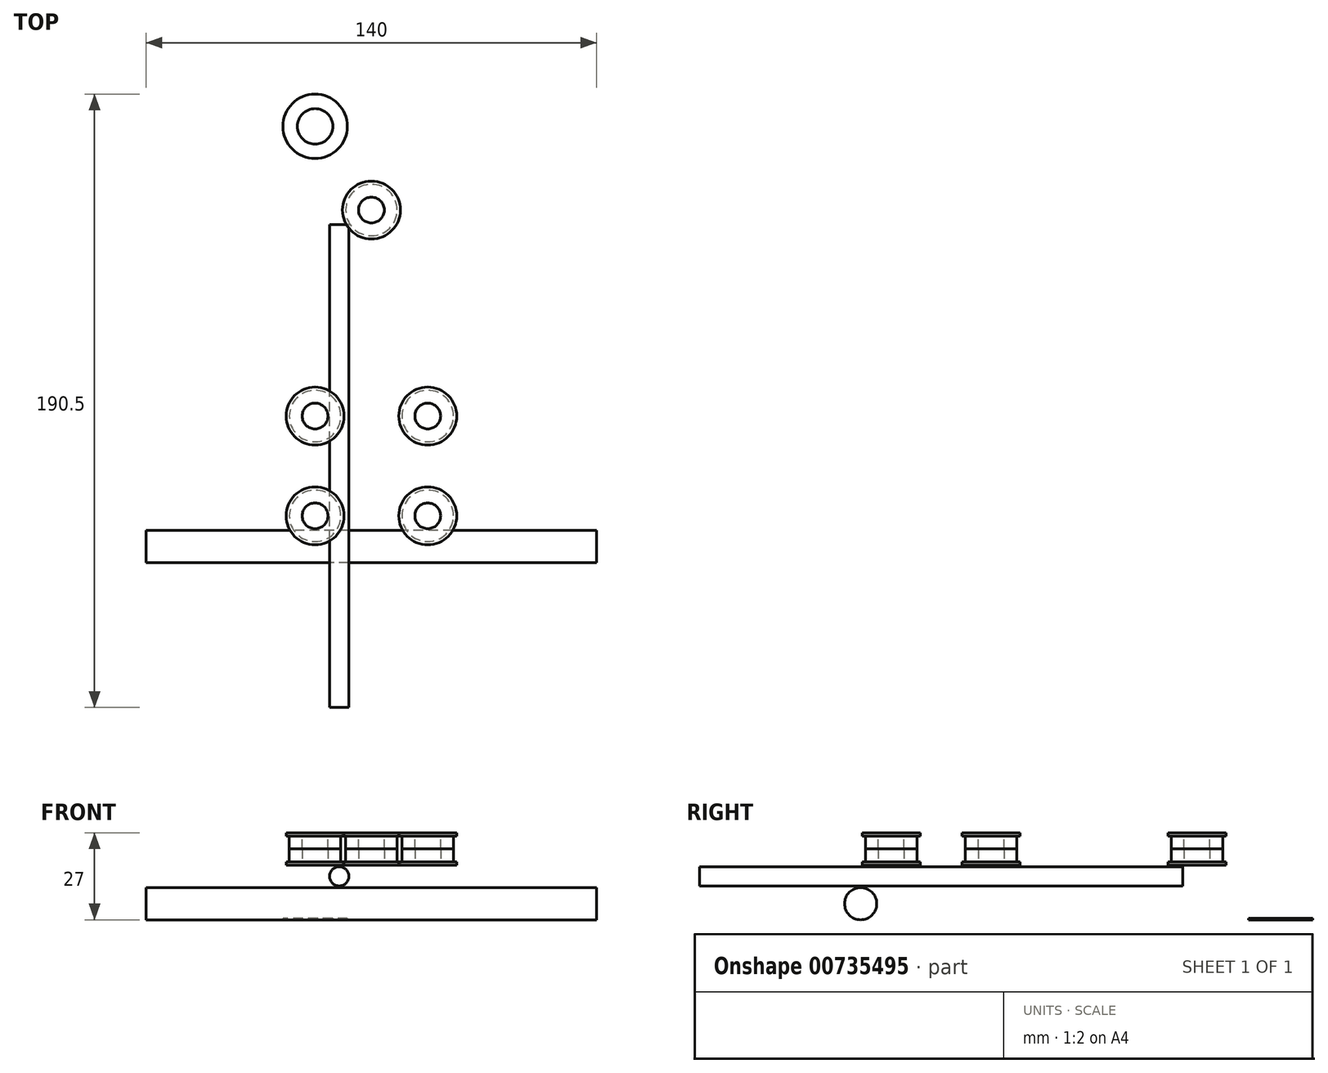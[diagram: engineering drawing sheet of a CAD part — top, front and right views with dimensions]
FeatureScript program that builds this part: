
annotation { "Feature Type Name" : "Feature", "Feature Type Description" : "" }
export const myFeature = defineFeature(function(context is Context, id is Id, definition is map)
    precondition{}
    {
        {
            var Q0;
            Q0=qCreatedBy(makeId("Right.planeOp"),FACE);
            var sketch = newSketch(context, id + "F0", { "sketchPlane" : qUnion([Q0])});
            skCircle(sketch, "E0", {"center": v(-25, 5) * mm, "radius": 5 * mm});
            skCircle(sketch, "E1.MirrorC", {"center": v(25, 5) * mm, "radius": 5 * mm});
            skCircle(sketch, "E2", {"center": v(-52.9, 19.58) * mm, "radius": 5 * mm});
            skCircle(sketch, "E3", {"center": v(-52.9, 19.58) * mm, "radius": 9.5 * mm});
            skCircle(sketch, "E4", {"center": v(-52.9, 19.58) * mm, "radius": 9.05 * mm});
            skSolve(sketch);
        }
        {
            var Q0;
            Q0=makeQuery(id+"F0.imprint","IMPRINT",FACE,{"disambiguationData":[TD([[makeQuery(id+"F0.imprint","IMPRINT",EDGE,{"derivedFrom":sQuery(id+"F0.wireOp",EDGE,"E0")}),1.0]])]});
            var Q1;
            Q1=makeQuery(id+"F0.imprint","IMPRINT",FACE,{"disambiguationData":[TD([[makeQuery(id+"F0.imprint","IMPRINT",EDGE,{"derivedFrom":sQuery(id+"F0.wireOp",EDGE,"E1.MirrorC")}),-1.0]])]});
            extrude(context, id + "F1", {"entities" : qUnion([Q0, Q1]), "endBound" : BoundingType.SYMMETRIC, "depth" : 140 * mm, "offsetDistance" : 25 * mm});
        }
        {
            var Q0;
            Q0=qCreatedBy(makeId("Front.planeOp"),FACE);
            var sketch = newSketch(context, id + "F2", { "sketchPlane" : qUnion([Q0])});
            skCircle(sketch, "E5", {"center": v(-10, 13.5) * mm, "radius": 3 * mm});
            skCircle(sketch, "E6.MirrorC", {"center": v(10, 13.5) * mm, "radius": 3 * mm});
            skLineSegment(sketch, "E7", {"start": v(-71.81, 0) * mm, "end": v(66.77, 0) * mm});
            skCircle(sketch, "E8", {"center": v(-31.3, 26.16) * mm, "radius": 3 * mm});
            skCircle(sketch, "E9", {"center": v(-31.3, 26.16) * mm, "radius": 5.7 * mm});
            skCircle(sketch, "E10", {"center": v(-31.3, 26.16) * mm, "radius": 6 * mm});
            skSolve(sketch);
        }
        {
            var Q0;
            Q0=makeQuery(id+"F2.imprint","IMPRINT",FACE,{"disambiguationData":[TD([[makeQuery(id+"F2.imprint","IMPRINT",EDGE,{"derivedFrom":sQuery(id+"F2.wireOp",EDGE,"E5")}),1.0]])]});
            var Q1;
            Q1=makeQuery(id+"F2.imprint","IMPRINT",FACE,{"disambiguationData":[TD([[makeQuery(id+"F2.imprint","IMPRINT",EDGE,{"derivedFrom":sQuery(id+"F2.wireOp",EDGE,"E6.MirrorC")}),-1.0]])]});
            extrude(context, id + "F3", {"entities" : qUnion([Q0, Q1]), "endBound" : BoundingType.SYMMETRIC, "depth" : 150 * mm, "offsetDistance" : 25 * mm});
        }
        {
            var Q0;
            Q0=qCreatedBy(makeId("Top.planeOp"),FACE);
            var sketch = newSketch(context, id + "F4", { "sketchPlane" : qUnion([Q0])});
            skCircle(sketch, "E11", {"center": v(-17.5, 15.5) * mm, "radius": 4 * mm});
            skCircle(sketch, "E12", {"center": v(-17.5, 15.5) * mm, "radius": 8 * mm});
            skCircle(sketch, "E13", {"center": v(-17.5, 15.5) * mm, "radius": 9 * mm});
            skCircle(sketch, "E14", {"center": v(-17.5, 15.5) * mm, "radius": 5.5 * mm});
            skCircle(sketch, "E15", {"center": v(-17.5, 15.5) * mm, "radius": 10 * mm});
            skSolve(sketch);
        }
        {
            var Q0;
            Q0=makeQuery(id+"F4.imprint","IMPRINT",FACE,{"disambiguationData":[TD([[makeQuery(id+"F4.imprint","IMPRINT",EDGE,{"derivedFrom":sQuery(id+"F4.wireOp",EDGE,"E12")}),-1.0]])]});
            extrude(context, id + "F5", {"entities" : qUnion([Q0]), "depth" : 1 * mm, "offsetDistance" : 25 * mm});
        }
        {
            var Q0;
            Q0=makeQuery(id+"F4.imprint","IMPRINT",FACE,{"disambiguationData":[TD([[makeQuery(id+"F4.imprint","IMPRINT",EDGE,{"derivedFrom":sQuery(id+"F4.wireOp",EDGE,"E11")}),-1.0]])]});
            var Q1;
            Q1=makeQuery(id+"F4.imprint","IMPRINT",FACE,{"disambiguationData":[TD([[makeQuery(id+"F4.imprint","IMPRINT",EDGE,{"derivedFrom":sQuery(id+"F4.wireOp",EDGE,"E12")}),1.0]])]});
            extrude(context, id + "F6", {"entities" : qUnion([Q0, Q1]), "operationType" : NewBodyOperationType.ADD, "depth" : 5 * mm, "offsetDistance" : 25 * mm});
        }
        {
            var Q0;
            Q0=makeQuery(id+"F5.opExtrude","SWEPT_BODY",BODY,{"disambiguationData":[OSD([sQuery(id+"F4.wireOp",EDGE,"E12"),sQuery(id+"F4.wireOp",EDGE,"E13")])]});
            transform(context, id + "F7", {"entities" : qUnion([Q0]), "transformType" : TransformType.TRANSLATION_3D, "dx" : 17.5 * 2 * mm, "dy" : 0 * mm, "dz" : 0 * mm, "makeCopy" : true});
        }
        {
            var Q0;
            Q0=makeQuery(id+"F5.opExtrude","SWEPT_BODY",BODY,{"disambiguationData":[OSD([sQuery(id+"F4.wireOp",EDGE,"E12"),sQuery(id+"F4.wireOp",EDGE,"E13")])]});
            var Q1;
            Q1=makeQuery(id+"F7.opPattern","COPY",BODY,{"derivedFrom":makeQuery(id+"F5.opExtrude","SWEPT_BODY",BODY,{"disambiguationData":[OSD([sQuery(id+"F4.wireOp",EDGE,"E12"),sQuery(id+"F4.wireOp",EDGE,"E13")])]}),"instanceName":"1"});
            transform(context, id + "F8", {"entities" : qUnion([Q0, Q1]), "transformType" : TransformType.TRANSLATION_3D, "dx" : 0 * mm, "dy" : -15.5 * 2 * mm, "dz" : 0 * mm, "makeCopy" : true});
        }
        {
            var Q0;
            Q0=makeQuery(id+"F5.opExtrude","SWEPT_BODY",BODY,{"disambiguationData":[OSD([sQuery(id+"F4.wireOp",EDGE,"E12"),sQuery(id+"F4.wireOp",EDGE,"E13")])]});
            var Q1;
            Q1=makeQuery(id+"F7.opPattern","COPY",BODY,{"derivedFrom":makeQuery(id+"F5.opExtrude","SWEPT_BODY",BODY,{"disambiguationData":[OSD([sQuery(id+"F4.wireOp",EDGE,"E12"),sQuery(id+"F4.wireOp",EDGE,"E13")])]}),"instanceName":"1"});
            var Q2;
            Q2=makeQuery(id+"F8.opPattern","COPY",BODY,{"derivedFrom":makeQuery(id+"F7.opPattern","COPY",BODY,{"derivedFrom":makeQuery(id+"F5.opExtrude","SWEPT_BODY",BODY,{"disambiguationData":[OSD([sQuery(id+"F4.wireOp",EDGE,"E12"),sQuery(id+"F4.wireOp",EDGE,"E13")])]}),"instanceName":"1"}),"instanceName":"1"});
            var Q3;
            Q3=makeQuery(id+"F8.opPattern","COPY",BODY,{"derivedFrom":makeQuery(id+"F5.opExtrude","SWEPT_BODY",BODY,{"disambiguationData":[OSD([sQuery(id+"F4.wireOp",EDGE,"E12"),sQuery(id+"F4.wireOp",EDGE,"E13")])]}),"instanceName":"1"});
            var Q4;
            Q4=sQuery(id+"F2.wireOp",EDGE,"E7");
            transform(context, id + "F9", {"entities" : qUnion([Q0, Q1, Q2, Q3]), "transformType" : TransformType.ROTATION, "transformAxis" : qUnion([Q4]), "angle" : 180 * degree, "makeCopy" : true});
        }
        {
            var Q0;
            Q0=makeQuery(id+"F9.opPattern","COPY",BODY,{"derivedFrom":makeQuery(id+"F8.opPattern","COPY",BODY,{"derivedFrom":makeQuery(id+"F5.opExtrude","SWEPT_BODY",BODY,{"disambiguationData":[OSD([sQuery(id+"F4.wireOp",EDGE,"E12"),sQuery(id+"F4.wireOp",EDGE,"E13")])]}),"instanceName":"1"}),"instanceName":"1"});
            var Q1;
            Q1=makeQuery(id+"F9.opPattern","COPY",BODY,{"derivedFrom":makeQuery(id+"F5.opExtrude","SWEPT_BODY",BODY,{"disambiguationData":[OSD([sQuery(id+"F4.wireOp",EDGE,"E12"),sQuery(id+"F4.wireOp",EDGE,"E13")])]}),"instanceName":"1"});
            var Q2;
            Q2=makeQuery(id+"F9.opPattern","COPY",BODY,{"derivedFrom":makeQuery(id+"F7.opPattern","COPY",BODY,{"derivedFrom":makeQuery(id+"F5.opExtrude","SWEPT_BODY",BODY,{"disambiguationData":[OSD([sQuery(id+"F4.wireOp",EDGE,"E12"),sQuery(id+"F4.wireOp",EDGE,"E13")])]}),"instanceName":"1"}),"instanceName":"1"});
            var Q3;
            Q3=makeQuery(id+"F9.opPattern","COPY",BODY,{"derivedFrom":makeQuery(id+"F8.opPattern","COPY",BODY,{"derivedFrom":makeQuery(id+"F7.opPattern","COPY",BODY,{"derivedFrom":makeQuery(id+"F5.opExtrude","SWEPT_BODY",BODY,{"disambiguationData":[OSD([sQuery(id+"F4.wireOp",EDGE,"E12"),sQuery(id+"F4.wireOp",EDGE,"E13")])]}),"instanceName":"1"}),"instanceName":"1"}),"instanceName":"1"});
            transform(context, id + "F10", {"entities" : qUnion([Q0, Q1, Q2, Q3]), "transformType" : TransformType.TRANSLATION_3D, "dx" : 0 * mm, "dy" : 0 * mm, "dz" : 27 * mm, "makeCopy" : false});
        }
        {
            var Q0;
            Q0=makeQuery(id+"F8.opPattern","COPY",BODY,{"derivedFrom":makeQuery(id+"F7.opPattern","COPY",BODY,{"derivedFrom":makeQuery(id+"F5.opExtrude","SWEPT_BODY",BODY,{"disambiguationData":[OSD([sQuery(id+"F4.wireOp",EDGE,"E12"),sQuery(id+"F4.wireOp",EDGE,"E13")])]}),"instanceName":"1"}),"instanceName":"1"});
            var Q1;
            Q1=makeQuery(id+"F7.opPattern","COPY",BODY,{"derivedFrom":makeQuery(id+"F5.opExtrude","SWEPT_BODY",BODY,{"disambiguationData":[OSD([sQuery(id+"F4.wireOp",EDGE,"E12"),sQuery(id+"F4.wireOp",EDGE,"E13")])]}),"instanceName":"1"});
            var Q2;
            Q2=makeQuery(id+"F5.opExtrude","SWEPT_BODY",BODY,{"disambiguationData":[OSD([sQuery(id+"F4.wireOp",EDGE,"E12"),sQuery(id+"F4.wireOp",EDGE,"E13")])]});
            var Q3;
            Q3=makeQuery(id+"F8.opPattern","COPY",BODY,{"derivedFrom":makeQuery(id+"F5.opExtrude","SWEPT_BODY",BODY,{"disambiguationData":[OSD([sQuery(id+"F4.wireOp",EDGE,"E12"),sQuery(id+"F4.wireOp",EDGE,"E13")])]}),"instanceName":"1"});
            transform(context, id + "F11", {"entities" : qUnion([Q0, Q1, Q2, Q3]), "transformType" : TransformType.TRANSLATION_3D, "dx" : 0 * mm, "dy" : 0 * mm, "dz" : 17 * mm, "makeCopy" : false});
        }
        {
            var Q0;
            Q0=makeQuery(id+"F9.opPattern","COPY",BODY,{"derivedFrom":makeQuery(id+"F8.opPattern","COPY",BODY,{"derivedFrom":makeQuery(id+"F5.opExtrude","SWEPT_BODY",BODY,{"disambiguationData":[OSD([sQuery(id+"F4.wireOp",EDGE,"E12"),sQuery(id+"F4.wireOp",EDGE,"E13")])]}),"instanceName":"1"}),"instanceName":"1"});
            transform(context, id + "F12", {"entities" : qUnion([Q0]), "transformType" : TransformType.TRANSLATION_3D, "dx" : 17.5 * mm, "dy" : 64 * mm, "dz" : 0 * mm, "makeCopy" : true});
        }
        {
            var Q0;
            Q0=makeQuery(id+"F12.opPattern","COPY",BODY,{"derivedFrom":makeQuery(id+"F9.opPattern","COPY",BODY,{"derivedFrom":makeQuery(id+"F8.opPattern","COPY",BODY,{"derivedFrom":makeQuery(id+"F5.opExtrude","SWEPT_BODY",BODY,{"disambiguationData":[OSD([sQuery(id+"F4.wireOp",EDGE,"E12"),sQuery(id+"F4.wireOp",EDGE,"E13")])]}),"instanceName":"1"}),"instanceName":"1"}),"instanceName":"1"});
            var Q1;
            Q1=sQuery(id+"F2.wireOp",EDGE,"E7");
            transform(context, id + "F13", {"entities" : qUnion([Q0]), "transformType" : TransformType.ROTATION, "transformAxis" : qUnion([Q1]), "angle" : 180 * degree, "makeCopy" : true});
        }
        {
            var Q0;
            Q0=makeQuery(id+"F13.opPattern","COPY",BODY,{"derivedFrom":makeQuery(id+"F12.opPattern","COPY",BODY,{"derivedFrom":makeQuery(id+"F9.opPattern","COPY",BODY,{"derivedFrom":makeQuery(id+"F8.opPattern","COPY",BODY,{"derivedFrom":makeQuery(id+"F5.opExtrude","SWEPT_BODY",BODY,{"disambiguationData":[OSD([sQuery(id+"F4.wireOp",EDGE,"E12"),sQuery(id+"F4.wireOp",EDGE,"E13")])]}),"instanceName":"1"}),"instanceName":"1"}),"instanceName":"1"}),"instanceName":"1"});
            transform(context, id + "F14", {"entities" : qUnion([Q0]), "transformType" : TransformType.TRANSLATION_3D, "dx" : 0 * mm, "dy" : 159 * mm, "dz" : 44 * mm, "makeCopy" : false});
        }
        {
            var Q0;
            Q0=makeQuery(id+"F13.opPattern","COPY",BODY,{"derivedFrom":makeQuery(id+"F12.opPattern","COPY",BODY,{"derivedFrom":makeQuery(id+"F9.opPattern","COPY",BODY,{"derivedFrom":makeQuery(id+"F8.opPattern","COPY",BODY,{"derivedFrom":makeQuery(id+"F5.opExtrude","SWEPT_BODY",BODY,{"disambiguationData":[OSD([sQuery(id+"F4.wireOp",EDGE,"E12"),sQuery(id+"F4.wireOp",EDGE,"E13")])]}),"instanceName":"1"}),"instanceName":"1"}),"instanceName":"1"}),"instanceName":"1"});
            var Q1;
            Q1=makeQuery(id+"F3.opExtrude","SWEPT_BODY",BODY,{"disambiguationData":[OSD([sQuery(id+"F2.wireOp",EDGE,"E5")])]});
            var Q2;
            Q2=makeQuery(id+"F12.opPattern","COPY",BODY,{"derivedFrom":makeQuery(id+"F9.opPattern","COPY",BODY,{"derivedFrom":makeQuery(id+"F8.opPattern","COPY",BODY,{"derivedFrom":makeQuery(id+"F5.opExtrude","SWEPT_BODY",BODY,{"disambiguationData":[OSD([sQuery(id+"F4.wireOp",EDGE,"E12"),sQuery(id+"F4.wireOp",EDGE,"E13")])]}),"instanceName":"1"}),"instanceName":"1"}),"instanceName":"1"});
            var Q3;
            Q3=makeQuery(id+"F7.opPattern","COPY",BODY,{"derivedFrom":makeQuery(id+"F5.opExtrude","SWEPT_BODY",BODY,{"disambiguationData":[OSD([sQuery(id+"F4.wireOp",EDGE,"E12"),sQuery(id+"F4.wireOp",EDGE,"E13")])]}),"instanceName":"1"});
            var Q4;
            Q4=makeQuery(id+"F3.opExtrude","SWEPT_BODY",BODY,{"disambiguationData":[OSD([sQuery(id+"F2.wireOp",EDGE,"E6.MirrorC")])]});
            var Q5;
            Q5=makeQuery(id+"F9.opPattern","COPY",BODY,{"derivedFrom":makeQuery(id+"F8.opPattern","COPY",BODY,{"derivedFrom":makeQuery(id+"F7.opPattern","COPY",BODY,{"derivedFrom":makeQuery(id+"F5.opExtrude","SWEPT_BODY",BODY,{"disambiguationData":[OSD([sQuery(id+"F4.wireOp",EDGE,"E12"),sQuery(id+"F4.wireOp",EDGE,"E13")])]}),"instanceName":"1"}),"instanceName":"1"}),"instanceName":"1"});
            var Q6;
            Q6=makeQuery(id+"F1.opExtrude","SWEPT_BODY",BODY,{"disambiguationData":[OSD([sQuery(id+"F0.wireOp",EDGE,"E1.MirrorC")])]});
            var Q7;
            Q7=makeQuery(id+"F1.opExtrude","SWEPT_BODY",BODY,{"disambiguationData":[OSD([sQuery(id+"F0.wireOp",EDGE,"E0")])]});
            var Q8;
            Q8=makeQuery(id+"F5.opExtrude","SWEPT_BODY",BODY,{"disambiguationData":[OSD([sQuery(id+"F4.wireOp",EDGE,"E12"),sQuery(id+"F4.wireOp",EDGE,"E13")])]});
            var Q9;
            Q9=makeQuery(id+"F8.opPattern","COPY",BODY,{"derivedFrom":makeQuery(id+"F5.opExtrude","SWEPT_BODY",BODY,{"disambiguationData":[OSD([sQuery(id+"F4.wireOp",EDGE,"E12"),sQuery(id+"F4.wireOp",EDGE,"E13")])]}),"instanceName":"1"});
            var Q10;
            Q10=makeQuery(id+"F8.opPattern","COPY",BODY,{"derivedFrom":makeQuery(id+"F7.opPattern","COPY",BODY,{"derivedFrom":makeQuery(id+"F5.opExtrude","SWEPT_BODY",BODY,{"disambiguationData":[OSD([sQuery(id+"F4.wireOp",EDGE,"E12"),sQuery(id+"F4.wireOp",EDGE,"E13")])]}),"instanceName":"1"}),"instanceName":"1"});
            var Q11;
            Q11=makeQuery(id+"F9.opPattern","COPY",BODY,{"derivedFrom":makeQuery(id+"F5.opExtrude","SWEPT_BODY",BODY,{"disambiguationData":[OSD([sQuery(id+"F4.wireOp",EDGE,"E12"),sQuery(id+"F4.wireOp",EDGE,"E13")])]}),"instanceName":"1"});
            var Q12;
            Q12=makeQuery(id+"F9.opPattern","COPY",BODY,{"derivedFrom":makeQuery(id+"F7.opPattern","COPY",BODY,{"derivedFrom":makeQuery(id+"F5.opExtrude","SWEPT_BODY",BODY,{"disambiguationData":[OSD([sQuery(id+"F4.wireOp",EDGE,"E12"),sQuery(id+"F4.wireOp",EDGE,"E13")])]}),"instanceName":"1"}),"instanceName":"1"});
            var Q13;
            Q13=makeQuery(id+"F9.opPattern","COPY",BODY,{"derivedFrom":makeQuery(id+"F8.opPattern","COPY",BODY,{"derivedFrom":makeQuery(id+"F5.opExtrude","SWEPT_BODY",BODY,{"disambiguationData":[OSD([sQuery(id+"F4.wireOp",EDGE,"E12"),sQuery(id+"F4.wireOp",EDGE,"E13")])]}),"instanceName":"1"}),"instanceName":"1"});
            var Q14;
            Q14=qCreatedBy(makeId("Front.planeOp"),FACE);
            transform(context, id + "F15", {"entities" : qUnion([Q0, Q1, Q2, Q3, Q4, Q5, Q6, Q7, Q8, Q9, Q10, Q11, Q12, Q13]), "transformType" : TransformType.TRANSLATION_DISTANCE, "transformDirection" : qUnion([Q14]), "distance" : 90 * mm, "makeCopy" : false});
        }
        {
            var Q0;
            Q0=makeQuery(id+"F4.imprint","IMPRINT",FACE,{"disambiguationData":[TD([[makeQuery(id+"F4.imprint","IMPRINT",EDGE,{"derivedFrom":sQuery(id+"F4.wireOp",EDGE,"E12")}),1.0]])]});
            var Q1;
            Q1=makeQuery(id+"F4.imprint","IMPRINT",FACE,{"disambiguationData":[TD([[makeQuery(id+"F4.imprint","IMPRINT",EDGE,{"derivedFrom":sQuery(id+"F4.wireOp",EDGE,"E12")}),-1.0]])]});
            var Q2;
            Q2=makeQuery(id+"F4.imprint","IMPRINT",FACE,{"disambiguationData":[TD([[makeQuery(id+"F4.imprint","IMPRINT",EDGE,{"derivedFrom":sQuery(id+"F4.wireOp",EDGE,"E13")}),-1.0]])]});
            extrude(context, id + "F16", {"entities" : qUnion([Q0, Q1, Q2]), "depth" : 0.5 * mm, "offsetDistance" : 25 * mm});
        }
    });
